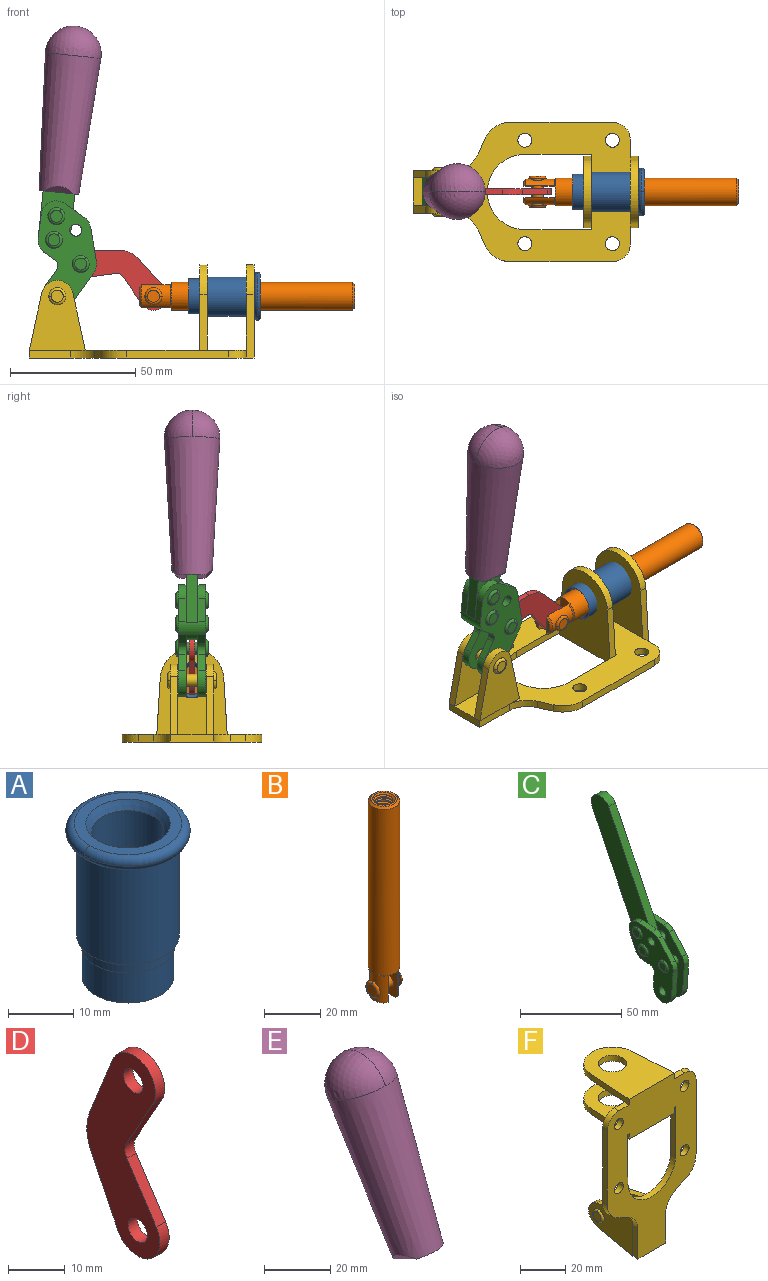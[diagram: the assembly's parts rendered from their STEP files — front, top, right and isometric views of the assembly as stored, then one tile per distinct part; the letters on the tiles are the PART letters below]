
ASSEMBLY  parts=6 mates=5
PART A: 15 faces, bbox 20.6x20.6x28.7 mm
  f0: torus R=8.26mm, axis (0,0,1), area 56.8mm2, adj f1,f10,f12
  f1: torus R=8.26mm, axis (0,0,1), area 56.8mm2, adj f0,f6,f13
  f2: cylinder r=5.59mm len=25.91mm, axis (0,0,1), area 909.6mm2, adj f3,f4
  f3: cone r=6.86mm half-angle=45deg, axis (0,0,-1), area 70.2mm2, adj f2,f14
  f4: cone r=6.47mm half-angle=30deg, axis (0,0,1), area 66.7mm2, adj f2,f13
  f5: cylinder r=7.04mm len=14.07mm, axis (0,0,1), area 252.6mm2, adj f11,f14
  f6: torus R=8.26mm, axis (0,0,1), area 56.8mm2, adj f1,f12,f13
  f7: cylinder r=7.16mm len=14.33mm, axis (0,0,1), area 91.5mm2, adj f9,f11
  f8: cylinder r=7.86mm len=18.42mm, axis (0,0,1), area 909.6mm2, adj f9,f10
  f9: plane 15.72x15.72mm, normal (0,0,-1), area 33mm2, adj f7,f8
  f10: plane 16.51x16.51mm, normal (0,0,-1), area 19.9mm2, adj f0,f8,f12
  f11: plane 14.33x14.33mm, normal (0,0,-1), area 5.7mm2, adj f5,f7
  f12: torus R=8.26mm, axis (0,0,1), area 56.8mm2, adj f0,f6,f10
  f13: plane 16.51x16.51mm, normal (0,0,1), area 82.7mm2, adj f1,f4,f6
  f14: plane 14.07x14.07mm, normal (0,0,-1), area 7.8mm2, adj f3,f5
PART B: 48 faces, bbox 12.6x11.1x86.1 mm
  f0: torus R=2.41mm, axis (-1,0,0), area 15mm2, adj f30,f32,f34
  f1: torus R=2.41mm, axis (-1,0,0), area 15mm2, adj f29,f31,f33
  f2: cylinder r=5.54mm len=72.39mm, axis (0,0,1), area 2518.5mm2, adj f3,f4,f42,f43
  f3: cone r=5.54mm half-angle=45deg, axis (0,0,1), area 7.6mm2, adj f2,f5,f41
  f4: cone r=5.54mm half-angle=45deg, axis (0,0,-1), area 34.9mm2, adj f2,f39
  f5: cylinder r=5.08mm len=11.48mm, axis (0,0,1), area 108.3mm2, adj f3,f7,f8,f41
  f6: cylinder r=2.41mm len=4.83mm, axis (-1,0,0), area 71.2mm2, adj f40,f41
  f7: cylinder r=2.41mm len=4.83mm, axis (-1,0,0), area 7.6mm2, adj f5,f34
  f8: cone r=5.08mm half-angle=45deg, axis (0,0,1), area 10.6mm2, adj f5,f37,f41
  f9: cone r=3.98mm half-angle=45deg, axis (0,0,1), area 17.6mm2, adj f27,f39,f45,f46,f47
  f10: cylinder r=2.41mm len=4.83mm, axis (-1,0,0), area 7.6mm2, adj f33,f38
  f11: cylinder r=3.2mm len=6.4mm, axis (0,0,1), area 78.4mm2, adj f12,f28,f44,f45,f47
  f12: cylinder r=3.2mm len=6.4mm, axis (0,0,1), area 10.5mm2, adj f11,f13,f45,f47
  f13: cylinder r=3.2mm len=6.4mm, axis (0,0,1), area 10.5mm2, adj f12,f14,f45,f47
  f14: cylinder r=3.2mm len=6.4mm, axis (0,0,1), area 10.5mm2, adj f13,f15,f45,f47
  f15: cylinder r=3.2mm len=6.4mm, axis (0,0,1), area 10.5mm2, adj f14,f16,f45,f47
  f16: cylinder r=3.2mm len=6.4mm, axis (0,0,1), area 10.5mm2, adj f15,f17,f45,f47
  f17: cylinder r=3.2mm len=6.4mm, axis (0,0,1), area 10.5mm2, adj f16,f18,f45,f47
  f18: cylinder r=3.2mm len=6.4mm, axis (0,0,1), area 10.5mm2, adj f17,f19,f45,f47
  f19: cylinder r=3.2mm len=6.4mm, axis (0,0,1), area 10.5mm2, adj f18,f20,f45,f47
  f20: cylinder r=3.2mm len=6.4mm, axis (0,0,1), area 10.5mm2, adj f19,f21,f45,f47
  f21: cylinder r=3.2mm len=6.4mm, axis (0,0,1), area 10.5mm2, adj f20,f22,f45,f47
  f22: cylinder r=3.2mm len=6.4mm, axis (0,0,1), area 10.5mm2, adj f21,f23,f45,f47
  f23: cylinder r=3.2mm len=6.4mm, axis (0,0,1), area 10.5mm2, adj f22,f24,f45,f47
  f24: cylinder r=3.2mm len=6.4mm, axis (0,0,1), area 10.5mm2, adj f23,f25,f45,f47
  f25: cylinder r=3.2mm len=6.4mm, axis (0,0,1), area 10.5mm2, adj f24,f26,f45,f47
  f26: cylinder r=3.2mm len=6.4mm, axis (0,0,1), area 10.5mm2, adj f25,f27,f45,f47
  f27: cylinder r=3.2mm len=6.4mm, axis (0,0,1), area 7.4mm2, adj f9,f26,f45,f47
  f28: cone r=3.2mm half-angle=60deg, axis (0,0,1), area 37.2mm2, adj f11
  f29: plane 4.83x4.83mm, normal (-1,0,0), area 18.3mm2, adj f1,f31
  f30: plane 4.83x4.83mm, normal (1,0,0), area 18.3mm2, adj f0,f32
  f31: torus R=2.41mm, axis (-1,0,0), area 15mm2, adj f1,f29,f33
  f32: torus R=2.41mm, axis (-1,0,0), area 15mm2, adj f0,f30,f34
  f33: plane 6.83x6.83mm, normal (1,0,0), area 18.3mm2, adj f1,f10,f31
  f34: plane 6.83x6.83mm, normal (-1,0,0), area 18.3mm2, adj f0,f7,f32
  f35: cone r=5.08mm half-angle=45deg, axis (0,0,1), area 10.6mm2, adj f36,f38,f40
  f36: plane 7.25x1.97mm, normal (0,0,-1), area 10mm2, adj f35,f40
  f37: plane 7.25x1.97mm, normal (0,0,-1), area 10mm2, adj f8,f41
  f38: cylinder r=5.08mm len=11.48mm, axis (0,0,1), area 108.3mm2, adj f10,f35,f40,f42
  f39: plane 9.55x9.55mm, normal (0,0,1), area 22mm2, adj f4,f9
  f40: plane 12.76x10.09mm, normal (1,0,0), area 95.7mm2, adj f6,f35,f36,f38,f42,f43
  f41: plane 12.76x10.09mm, normal (-1,0,0), area 95.7mm2, adj f3,f5,f6,f8,f37,f43
  f42: cone r=5.54mm half-angle=45deg, axis (0,0,1), area 7.6mm2, adj f2,f38,f40
  f43: plane 11.07x4.7mm, normal (0,0,-1), area 50.4mm2, adj f2,f40,f41
  f44: plane 0.89x0.62mm, normal (-1,0,0), area 0.3mm2, adj f11,f45,f46,f47
  f45: bspline ~24.8x7.63mm, area 266.6mm2, adj f9,f11,f12,f13,f14,f15,f16,f17
  f46: bspline ~24.87x7.63mm, area 73.6mm2, adj f9,f44,f45,f47
  f47: bspline ~24.98x7.63mm, area 272.5mm2, adj f9,f11,f12,f13,f14,f15,f16,f17
PART C: 59 faces, bbox 12.9x60.2x99.6 mm
  f0: torus R=2.39mm, axis (-1,0,0), area 14.9mm2, adj f20,f43,f51
  f1: torus R=2.39mm, axis (-1,0,0), area 14.9mm2, adj f19,f42,f51
  f2: torus R=2.39mm, axis (-1,0,0), area 14.9mm2, adj f18,f35,f51
  f3: torus R=2.39mm, axis (-1,0,0), area 14.9mm2, adj f14,f17,f23
  f4: torus R=2.39mm, axis (-1,0,0), area 14.9mm2, adj f13,f16,f23
  f5: torus R=2.39mm, axis (-1,0,0), area 14.9mm2, adj f12,f15,f23
  f6: cylinder r=2.39mm len=4.78mm, axis (1,0,0), area 46.5mm2, adj f48,f50,f51
  f7: cylinder r=2.39mm len=4.78mm, axis (1,0,0), area 46.5mm2, adj f50,f51
  f8: cylinder r=6.35mm len=12.68mm, axis (1,0,0), area 61.8mm2, adj f38,f39,f50,f51
  f9: cylinder r=2.39mm len=4.78mm, axis (-1,0,0), area 70.5mm2, adj f46,f50
  f10: cylinder r=2.39mm len=4.78mm, axis (-1,0,0), area 46.5mm2, adj f23,f45,f46
  f11: cylinder r=2.39mm len=4.78mm, axis (-1,0,0), area 46.5mm2, adj f23,f46
  f12: plane 4.78x4.78mm, normal (1,0,0), area 17.9mm2, adj f5,f15
  f13: plane 4.78x4.78mm, normal (1,0,0), area 17.9mm2, adj f4,f16
  f14: plane 4.78x4.78mm, normal (1,0,0), area 17.9mm2, adj f3,f17
  f15: torus R=2.39mm, axis (-1,0,0), area 14.9mm2, adj f5,f12,f23
  f16: torus R=2.39mm, axis (-1,0,0), area 14.9mm2, adj f4,f13,f23
  f17: torus R=2.39mm, axis (-1,0,0), area 14.9mm2, adj f3,f14,f23
  f18: plane 4.78x4.78mm, normal (-1,0,0), area 17.9mm2, adj f2,f35
  f19: plane 4.78x4.78mm, normal (-1,0,0), area 17.9mm2, adj f1,f42
  f20: plane 4.78x4.78mm, normal (-1,0,0), area 17.9mm2, adj f0,f43
  f21: plane 2.26x0.2mm, normal (1,0,0), area 0.2mm2, adj f31,f44
  f22: plane 2.26x0.2mm, normal (-1,0,0), area 0.2mm2, adj f41,f44
  f23: plane 39.37x30.77mm, normal (1,0,0), area 565.5mm2, adj f3,f4,f5,f10,f11,f15,f16,f17
  f24: cylinder r=6.1mm len=4.15mm, axis (-1,0,0), area 14.7mm2, adj f23,f25,f32,f46
  f25: plane 10.25x9.01mm, normal (0,-0.75,0.66), area 42.3mm2, adj f23,f24,f26,f46
  f26: cylinder r=6.35mm len=4.64mm, axis (-1,0,0), area 15.6mm2, adj f23,f25,f27,f46
  f27: plane 15.84x3.1mm, normal (0,-1,-0.07), area 49.2mm2, adj f23,f26,f28,f46
  f28: cylinder r=6.35mm len=12.68mm, axis (-1,0,0), area 61.8mm2, adj f23,f27,f29,f46
  f29: plane 8.11x3.1mm, normal (0,1,0.07), area 25.2mm2, adj f23,f28,f30,f46
  f30: cylinder r=3.05mm len=3.25mm, axis (-1,0,0), area 14.8mm2, adj f23,f29,f31,f46
  f31: plane 5.99x3.1mm, normal (0,0.07,-1), area 18.6mm2, adj f21,f23,f30,f44,f46
  f32: plane 9.5x3.1mm, normal (0,-0.07,1), area 29.5mm2, adj f23,f24,f33,f46,f47
  f33: cylinder r=6.1mm len=8.63mm, axis (-1,0,0), area 39.1mm2, adj f23,f32,f34,f47
  f34: plane 8.65x3.96mm, normal (0,0.91,-0.42), area 29.5mm2, adj f23,f33,f44,f47
  f35: torus R=2.39mm, axis (-1,0,0), area 14.9mm2, adj f2,f18,f51
  f36: plane 10.25x9.01mm, normal (0,-0.75,0.66), area 42.3mm2, adj f37,f49,f50,f51
  f37: cylinder r=6.35mm len=4.64mm, axis (1,0,0), area 15.6mm2, adj f36,f38,f50,f51
  f38: plane 15.84x3.1mm, normal (0,-1,-0.07), area 49.2mm2, adj f8,f37,f50,f51
  f39: plane 8.11x3.1mm, normal (0,1,0.07), area 25.2mm2, adj f8,f40,f50,f51
  f40: cylinder r=3.05mm len=3.25mm, axis (1,0,0), area 14.8mm2, adj f39,f41,f50,f51
  f41: plane 5.99x3.1mm, normal (0,0.07,-1), area 18.6mm2, adj f22,f40,f44,f50,f51
  f42: torus R=2.39mm, axis (-1,0,0), area 14.9mm2, adj f1,f19,f51
  f43: torus R=2.39mm, axis (-1,0,0), area 14.9mm2, adj f0,f20,f51
  f44: cylinder r=6.35mm len=12.12mm, axis (-1,0,0), area 128.9mm2, adj f21,f22,f23,f31,f34,f41,f46,f47
  f45: plane 2.65x1.35mm, normal (1,0,0), area 1mm2, adj f10,f55
  f46: plane 39.08x20.42mm, normal (-1,0,0), area 412.5mm2, adj f9,f10,f11,f24,f25,f26,f27,f28
  f47: plane 77.62x39.82mm, normal (1,0,0), area 850mm2, adj f32,f33,f34,f44,f53,f54,f55
  f48: plane 2.65x1.35mm, normal (-1,0,0), area 1mm2, adj f6,f55
  f49: cylinder r=6.1mm len=4.15mm, axis (1,0,0), area 14.7mm2, adj f36,f50,f51,f56
  f50: plane 39.08x20.42mm, normal (1,0,0), area 412.5mm2, adj f6,f7,f8,f9,f36,f37,f38,f39
  f51: plane 39.37x30.77mm, normal (-1,0,0), area 565.5mm2, adj f0,f1,f2,f6,f7,f8,f35,f36
  f52: plane 8.65x3.96mm, normal (0,0.91,-0.42), area 29.5mm2, adj f44,f51,f57,f58
  f53: plane 68.49x33.4mm, normal (0,0.9,-0.44), area 358.1mm2, adj f44,f47,f54,f58
  f54: cylinder r=6.35mm len=12.06mm, axis (1,0,0), area 93.7mm2, adj f47,f53,f55,f58
  f55: plane 68.49x33.4mm, normal (0,-0.9,0.44), area 358.1mm2, adj f44,f45,f46,f47,f48,f50,f54,f58
  f56: plane 9.5x3.1mm, normal (0,-0.07,1), area 29.5mm2, adj f49,f50,f51,f57,f58
  f57: cylinder r=6.1mm len=8.63mm, axis (1,0,0), area 39.1mm2, adj f51,f52,f56,f58
  f58: plane 77.62x39.82mm, normal (-1,0,0), area 850mm2, adj f44,f52,f53,f54,f55,f56,f57
PART D: 12 faces, bbox 2.3x18.2x42.8 mm
  f0: cylinder r=2.4mm len=4.8mm, axis (1,0,0), area 34.9mm2, adj f4,f11
  f1: cylinder r=10.41mm len=8.47mm, axis (1,0,0), area 20.2mm2, adj f4,f9,f10,f11
  f2: cylinder r=3.05mm len=3.16mm, axis (1,0,0), area 7.7mm2, adj f4,f6,f7,f11
  f3: cylinder r=2.4mm len=4.8mm, axis (1,0,0), area 34.9mm2, adj f4,f11
  f4: plane 42.81x18.23mm, normal (-1,0,0), area 414.1mm2, adj f0,f1,f2,f3,f5,f6,f7,f8
  f5: cylinder r=5.54mm len=10.67mm, axis (1,0,0), area 41.8mm2, adj f4,f6,f10,f11
  f6: plane 11.66x6.53mm, normal (0,-0.87,-0.49), area 30.9mm2, adj f2,f4,f5,f11
  f7: plane 11.17x7.33mm, normal (0,-0.84,0.55), area 30.9mm2, adj f2,f4,f8,f11
  f8: cylinder r=5.54mm len=10.51mm, axis (1,0,0), area 41.8mm2, adj f4,f7,f9,f11
  f9: plane 13.67x6.67mm, normal (0,0.9,-0.44), area 35.1mm2, adj f1,f4,f8,f11
  f10: plane 14.1x5.7mm, normal (0,0.93,0.37), area 35.1mm2, adj f1,f4,f5,f11
  f11: plane 42.81x18.23mm, normal (1,0,0), area 414.1mm2, adj f0,f1,f2,f3,f5,f6,f7,f8
PART E: 11 faces, bbox 22.3x42.6x64.5 mm
  f0: sphere r=11.13mm, area 411.4mm2, adj f1,f8
  f1: cone r=11.11mm half-angle=3.3deg, axis (0,0.44,0.9), area 3251.8mm2, adj f0,f7,f8,f9,f10
  f2: cylinder r=6.16mm len=11.7mm, axis (1,0,0), area 89.5mm2, adj f3,f4,f5,f6
  f3: plane 60.23x36.75mm, normal (-1,0,0), area 763.6mm2, adj f2,f4,f6,f10
  f4: plane 51.37x25.05mm, normal (0,0.9,-0.44), area 264.2mm2, adj f2,f3,f5,f10
  f5: plane 60.23x36.75mm, normal (1,0,0), area 763.6mm2, adj f2,f4,f6,f10
  f6: plane 51.37x25.05mm, normal (0,-0.9,0.44), area 264.2mm2, adj f2,f3,f5,f10
  f7: plane 9.95x5.95mm, normal (0.71,-0.31,-0.64), area 25.8mm2, adj f1,f10
  f8: sphere r=11.13mm, area 411.4mm2, adj f0,f1
  f9: plane 9.95x5.95mm, normal (-0.71,-0.31,-0.64), area 25.8mm2, adj f1,f10
  f10: plane 14.27x11.38mm, normal (0,-0.44,-0.9), area 106.7mm2, adj f1,f3,f4,f5,f6,f7,f9
PART F: 55 faces, bbox 55.7x37.4x89.8 mm
  f0: torus R=2.41mm, axis (-1,0,0), area 15mm2, adj f11,f15,f25
  f1: torus R=2.41mm, axis (-1,0,0), area 15mm2, adj f10,f12,f22
  f2: cylinder r=2.78mm len=5.56mm, axis (0,-1,0), area 54.2mm2, adj f30,f54
  f3: cylinder r=14.99mm len=29.97mm, axis (0,-1,0), area 145.9mm2, adj f30,f49,f53,f54
  f4: cylinder r=2.78mm len=5.56mm, axis (0,-1,0), area 54.2mm2, adj f30,f54
  f5: cylinder r=2.78mm len=5.56mm, axis (0,-1,0), area 54.2mm2, adj f30,f54
  f6: cylinder r=2.78mm len=5.56mm, axis (0,-1,0), area 54.2mm2, adj f30,f54
  f7: cylinder r=6.35mm len=12.7mm, axis (0,0,1), area 123.6mm2, adj f27,f51
  f8: cylinder r=6.35mm len=12.7mm, axis (0,0,-1), area 124.7mm2, adj f21,f35
  f9: cylinder r=2.41mm len=11.18mm, axis (-1,0,0), area 169.4mm2, adj f16,f19
  f10: plane 4.83x4.83mm, normal (1,0,0), area 18.3mm2, adj f1,f12
  f11: plane 4.83x4.83mm, normal (-1,0,0), area 18.3mm2, adj f0,f15
  f12: torus R=2.41mm, axis (-1,0,0), area 15mm2, adj f1,f10,f22
  f13: cylinder r=6.35mm len=12.41mm, axis (1,0,0), area 53.4mm2, adj f18,f19,f22,f23
  f14: cylinder r=6.35mm len=12.41mm, axis (-1,0,0), area 53.4mm2, adj f16,f17,f24,f25
  f15: torus R=2.41mm, axis (-1,0,0), area 15mm2, adj f0,f11,f25
  f16: plane 27.86x22.35mm, normal (1,0,0), area 425.4mm2, adj f9,f14,f17,f24,f30
  f17: plane 22.86x4.97mm, normal (0,0.21,0.98), area 72.5mm2, adj f14,f16,f25,f30
  f18: plane 22.86x4.97mm, normal (0,0.21,0.98), area 72.5mm2, adj f13,f19,f22,f30
  f19: plane 27.86x22.35mm, normal (-1,0,0), area 425.4mm2, adj f9,f13,f18,f23,f30
  f20: cylinder r=12.7mm len=25.35mm, axis (0,0,-1), area 119.8mm2, adj f21,f34,f35,f36
  f21: plane 34.21x28.07mm, normal (0,0,-1), area 702.4mm2, adj f8,f20,f30,f34,f36
  f22: plane 27.96x22.45mm, normal (1,0,0), area 407.2mm2, adj f1,f12,f13,f18,f23,f30,f42,f43
  f23: plane 22.86x4.97mm, normal (0,0.21,-0.98), area 72.5mm2, adj f13,f19,f22,f44
  f24: plane 22.86x4.97mm, normal (0,0.21,-0.98), area 72.5mm2, adj f14,f16,f25,f44
  f25: plane 27.86x22.35mm, normal (-1,0,0), area 407.1mm2, adj f0,f14,f15,f17,f24,f30,f45,f46
  f26: plane 3.1x0.95mm, normal (0,0,-1), area 2.7mm2, adj f30,f49,f50,f54
  f27: plane 34.21x28.07mm, normal (0,0,1), area 702.4mm2, adj f7,f28,f30,f50,f52
  f28: cylinder r=12.7mm len=25.35mm, axis (0,0,1), area 118.8mm2, adj f27,f50,f51,f52
  f29: plane 3.1x0.95mm, normal (0,0,-1), area 2.7mm2, adj f30,f52,f53,f54
  f30: plane 86.54x55.63mm, normal (0,1,0), area 2362.9mm2, adj f2,f3,f4,f5,f6,f16,f17,f18
  f31: plane 40.56x3.1mm, normal (-1,0,0), area 125.7mm2, adj f30,f32,f48,f54
  f32: cylinder r=7.11mm len=7.11mm, axis (0,-1,0), area 34.6mm2, adj f30,f31,f33,f54
  f33: plane 6.67x3.1mm, normal (0,0,1), area 20.4mm2, adj f30,f32,f34,f54
  f34: plane 25.39x3.13mm, normal (-1,0.06,0), area 79.5mm2, adj f20,f21,f33,f35,f54
  f35: plane 37.31x28.45mm, normal (0,0,1), area 789.9mm2, adj f8,f20,f34,f36,f54
  f36: plane 25.39x3.13mm, normal (1,0.06,0), area 79.5mm2, adj f20,f21,f35,f37,f54
  f37: plane 6.67x3.1mm, normal (0,0,1), area 20.4mm2, adj f30,f36,f38,f54
  f38: cylinder r=7.11mm len=7.11mm, axis (0,-1,0), area 34.6mm2, adj f30,f37,f39,f54
  f39: plane 40.56x3.1mm, normal (1,0,0), area 125.7mm2, adj f30,f38,f40,f54
  f40: cylinder r=11.18mm len=10.16mm, axis (0,-1,0), area 39.5mm2, adj f30,f39,f41,f54
  f41: plane 6.09x3.1mm, normal (0.42,0,-0.91), area 20.8mm2, adj f30,f40,f42,f54
  f42: cylinder r=11.18mm len=9.41mm, axis (0,-1,0), area 37.2mm2, adj f22,f30,f41,f43,f54
  f43: plane 16.5x3.1mm, normal (1,0,0), area 51.1mm2, adj f22,f42,f44,f54
  f44: plane 17.37x3.1mm, normal (0,0,-1), area 53.8mm2, adj f23,f24,f30,f43,f45,f54
  f45: plane 16.5x3.1mm, normal (-1,0,0), area 51.1mm2, adj f25,f44,f46,f54
  f46: cylinder r=11.18mm len=9.41mm, axis (0,-1,0), area 37.2mm2, adj f25,f30,f45,f47,f54
  f47: plane 6.09x3.1mm, normal (-0.42,0,-0.91), area 20.8mm2, adj f30,f46,f48,f54
  f48: cylinder r=11.18mm len=10.16mm, axis (0,-1,0), area 39.5mm2, adj f30,f31,f47,f54
  f49: plane 26.54x3.1mm, normal (-1,0,0), area 82.3mm2, adj f3,f26,f30,f54
  f50: plane 25.39x3.1mm, normal (1,0.06,0), area 78.8mm2, adj f26,f27,f28,f51,f54
  f51: plane 37.31x28.45mm, normal (0,0,-1), area 789.9mm2, adj f7,f28,f50,f52,f54
  f52: plane 25.39x3.1mm, normal (-1,0.06,0), area 78.8mm2, adj f27,f28,f29,f51,f54
  f53: plane 26.54x3.1mm, normal (1,0,0), area 82.3mm2, adj f3,f29,f30,f54
  f54: plane 89.66x55.63mm, normal (0,-1,0), area 2678.5mm2, adj f2,f3,f4,f5,f6,f26,f29,f31
PLACE A rot(axis=(0,1,0),90deg) t=(-1.23,-24.61,24.61)mm
PLACE B rot(axis=(0.58,0.58,0.58),120deg) t=(-10.45,0,0)mm
PLACE C rot(axis=(0.27,0.27,0.93),94.3deg) t=(4.54,0,38.82)mm
PLACE D rot(axis=(0.65,0.65,0.4),135.9deg) t=(-19.64,0,9.22)mm
PLACE E rot(axis=(0.27,0.27,0.93),94.3deg) t=(4.54,-0.04,38.82)mm
PLACE F rot(axis=(0.58,0.58,0.58),120deg) t=(-1.23,0,0)mm fixed
MATE slider B.f2 <-> A.f2  axis (1,0,0) through (48.33,0,24.61)mm
MATE fastened E.f2 <-> C.f54  axis (0,1,0) through (-26.76,-2.35,122.89)mm
MATE revolute C.f7 <-> F.f0  axis (0,1,0) through (-33.32,0,24.61)mm
MATE revolute D.f3 <-> C.f4  axis (0,1,0) through (-24.01,0,37.46)mm
MATE revolute D.f5 <-> B.f6  axis (0,1,0) through (5.03,0,24.61)mm
